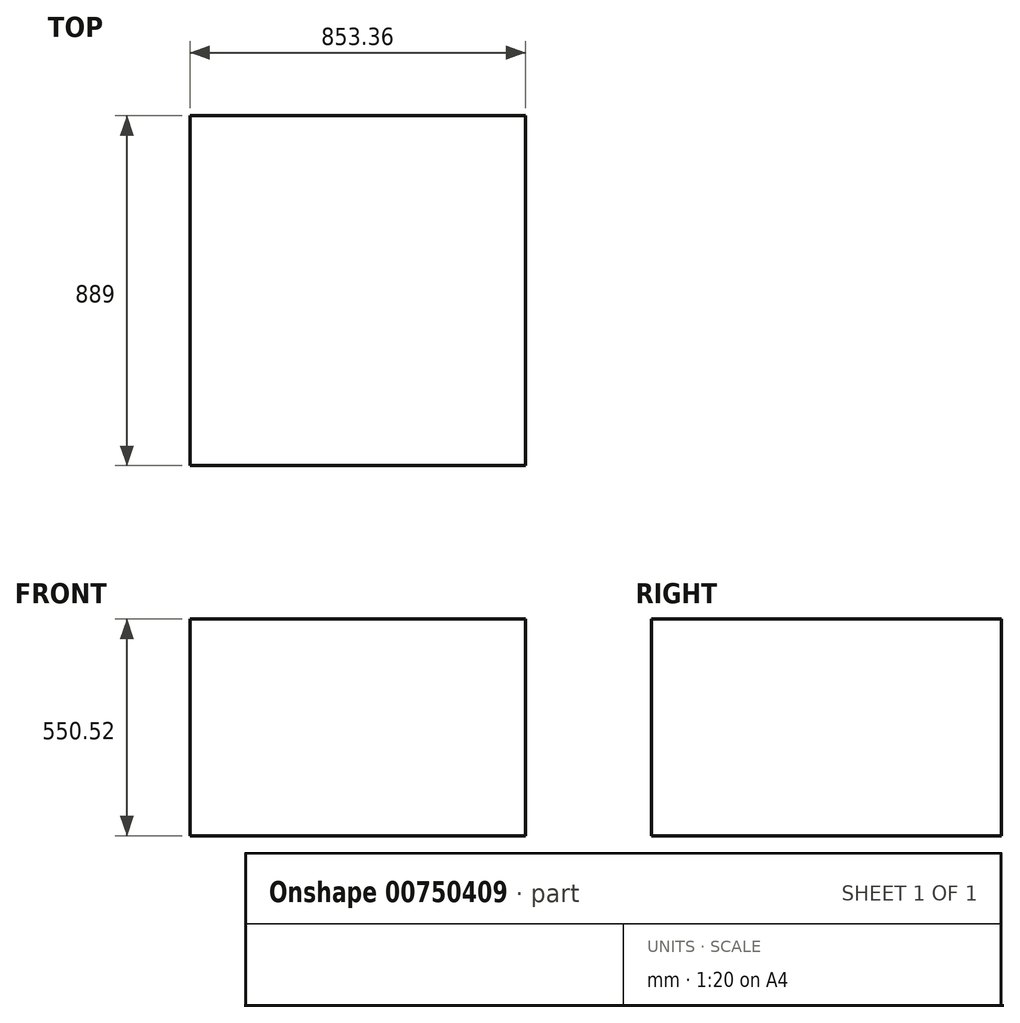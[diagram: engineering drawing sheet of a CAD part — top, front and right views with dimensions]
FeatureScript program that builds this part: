
annotation { "Feature Type Name" : "Feature", "Feature Type Description" : "" }
export const myFeature = defineFeature(function(context is Context, id is Id, definition is map)
    precondition{}
    {
        {
            var Q0;
            Q0=qCreatedBy(makeId("Front.planeOp"),FACE);
            var sketch = newSketch(context, id + "F0", { "sketchPlane" : qUnion([Q0])});
            skLineSegment(sketch, "E0.bottom", {"start": v(0, 0) * mm, "end": v(-853.36, 0) * mm});
            skLineSegment(sketch, "E0.top", {"start": v(0, 550.52) * mm, "end": v(-853.36, 550.52) * mm});
            skLineSegment(sketch, "E0.left", {"start": v(0, 0) * mm, "end": v(0, 550.52) * mm});
            skLineSegment(sketch, "E0.right", {"start": v(-853.36, 0) * mm, "end": v(-853.36, 550.52) * mm});
            skSolve(sketch);
        }
        {
            var Q0;
            Q0 = qSketchRegion(id + "F0", true);
            extrude(context, id + "F1", {"entities" : qUnion([Q0]), "depth" : 889 * mm, "offsetDistance" : 25.4 * mm});
        }
    });
